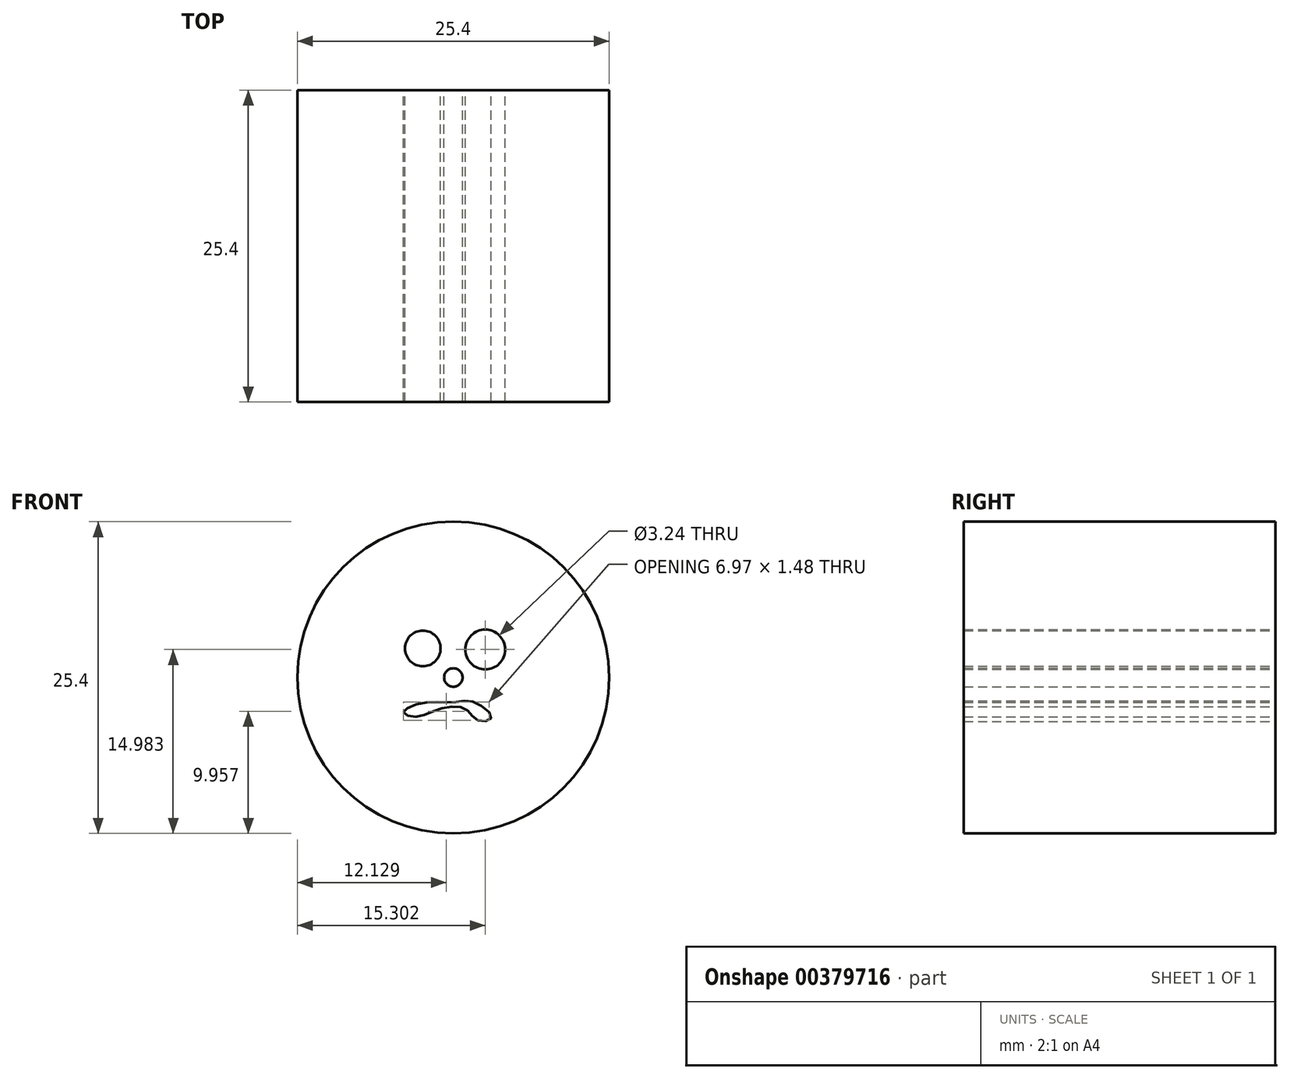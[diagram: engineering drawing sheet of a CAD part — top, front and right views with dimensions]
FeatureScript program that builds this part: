
annotation { "Feature Type Name" : "Feature", "Feature Type Description" : "" }
export const myFeature = defineFeature(function(context is Context, id is Id, definition is map)
    precondition{}
    {
        {
            var Q0;
            Q0=qCreatedBy(makeId("Front.planeOp"),FACE);
            var sketch = newSketch(context, id + "F0", { "sketchPlane" : qUnion([Q0])});
            skCircle(sketch, "E0", {"center": v(0, 0) * mm, "radius": 12.7 * mm});
            skCircle(sketch, "E1", {"center": v(-2.49, 2.37) * mm, "radius": 1.45 * mm});
            skCircle(sketch, "E2", {"center": v(2.6, 2.28) * mm, "radius": 1.62 * mm});
            skCircle(sketch, "E3", {"center": v(0, 0) * mm, "radius": 0.75 * mm});
            skFitSpline(sketch, "E4", {"points": [v(-4.06, -2.84) * mm, v(-2.55, -2.07) * mm, v(0, -2) * mm, v(1.8, -2.04) * mm, v(3.08, -3.3) * mm, v(1.98, -3.49) * mm, v(1.03, -2.6) * mm, v(-0.95, -2.51) * mm, v(-3, -3.2) * mm, v(-4.06, -2.84) * mm]});
            skSolve(sketch);
        }
        {
            var Q0;
            Q0=makeQuery(id+"F0.imprint","IMPRINT",FACE,{"disambiguationData":[TD([[makeQuery(id+"F0.imprint","IMPRINT",EDGE,{"derivedFrom":sQuery(id+"F0.wireOp",EDGE,"E0")}),1.0]])]});
            extrude(context, id + "F1", {"entities" : qUnion([Q0]), "depth" : 25.4 * mm});
        }
    });
